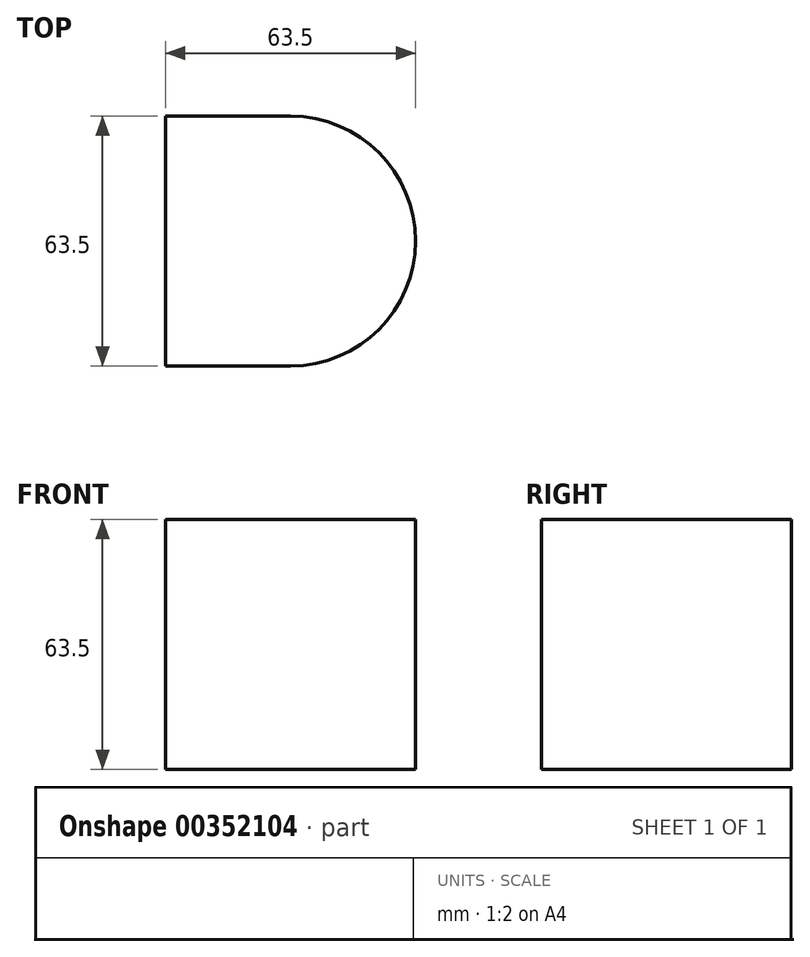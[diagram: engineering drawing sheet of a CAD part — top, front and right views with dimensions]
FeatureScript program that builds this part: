
annotation { "Feature Type Name" : "Feature", "Feature Type Description" : "" }
export const myFeature = defineFeature(function(context is Context, id is Id, definition is map)
    precondition{}
    {
        {
            var Q0;
            Q0=qCreatedBy(makeId("Top.planeOp"),FACE);
            var sketch = newSketch(context, id + "F0", { "sketchPlane" : qUnion([Q0])});
            skCircle(sketch, "E0", {"center": v(0, 0) * mm, "radius": 31.75 * mm});
            skLineSegment(sketch, "E1.bottom", {"start": v(0, 31.75) * mm, "end": v(-31.75, 31.75) * mm});
            skLineSegment(sketch, "E1.top", {"start": v(0, -31.75) * mm, "end": v(-31.75, -31.75) * mm});
            skLineSegment(sketch, "E1.left", {"start": v(0, 31.75) * mm, "end": v(0, -31.75) * mm});
            skLineSegment(sketch, "E1.right", {"start": v(-31.75, 31.75) * mm, "end": v(-31.75, -31.75) * mm});
            skSolve(sketch);
        }
        {
            var Q0;
            Q0 = qSketchRegion(id + "F0", true);
            extrude(context, id + "F1", {"entities" : qUnion([Q0]), "depth" : 63.5 * mm});
        }
    });
